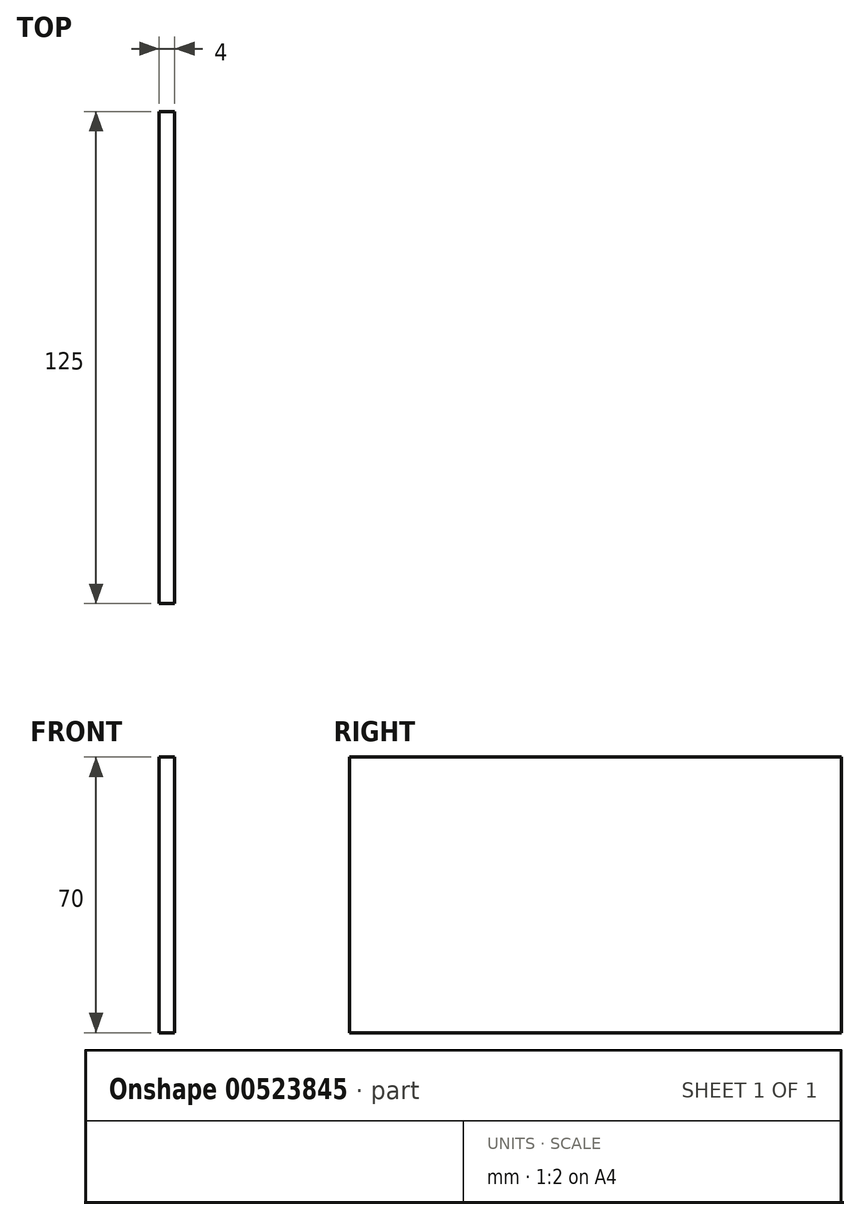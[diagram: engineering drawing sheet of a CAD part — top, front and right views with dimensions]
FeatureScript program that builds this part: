
annotation { "Feature Type Name" : "Feature", "Feature Type Description" : "" }
export const myFeature = defineFeature(function(context is Context, id is Id, definition is map)
    precondition{}
    {
        {
            var Q0;
            Q0=qCreatedBy(makeId("Right.planeOp"),FACE);
            var sketch = newSketch(context, id + "F0", { "sketchPlane" : qUnion([Q0])});
            skLineSegment(sketch, "E0.bottom", {"start": v(-62.5, 35) * mm, "end": v(62.5, 35) * mm});
            skLineSegment(sketch, "E0.top", {"start": v(-62.5, -35) * mm, "end": v(62.5, -35) * mm});
            skLineSegment(sketch, "E0.left", {"start": v(-62.5, 35) * mm, "end": v(-62.5, -35) * mm});
            skLineSegment(sketch, "E0.right", {"start": v(62.5, 35) * mm, "end": v(62.5, -35) * mm});
            skPoint(sketch, "E0.middle", {"position": v(0, 0) * mm});
            skSolve(sketch);
        }
        {
            var Q0;
            Q0=makeQuery(id+"F0.imprint","IMPRINT",FACE,{"disambiguationData":[TD([[makeQuery(id+"F0.imprint","IMPRINT",EDGE,{"derivedFrom":sQuery(id+"F0.wireOp",EDGE,"E0.bottom")}),-1.0]])]});
            extrude(context, id + "F1", {"entities" : qUnion([Q0]), "endBound" : BoundingType.SYMMETRIC, "depth" : 4 * mm, "offsetDistance" : 25 * mm});
        }
    });
